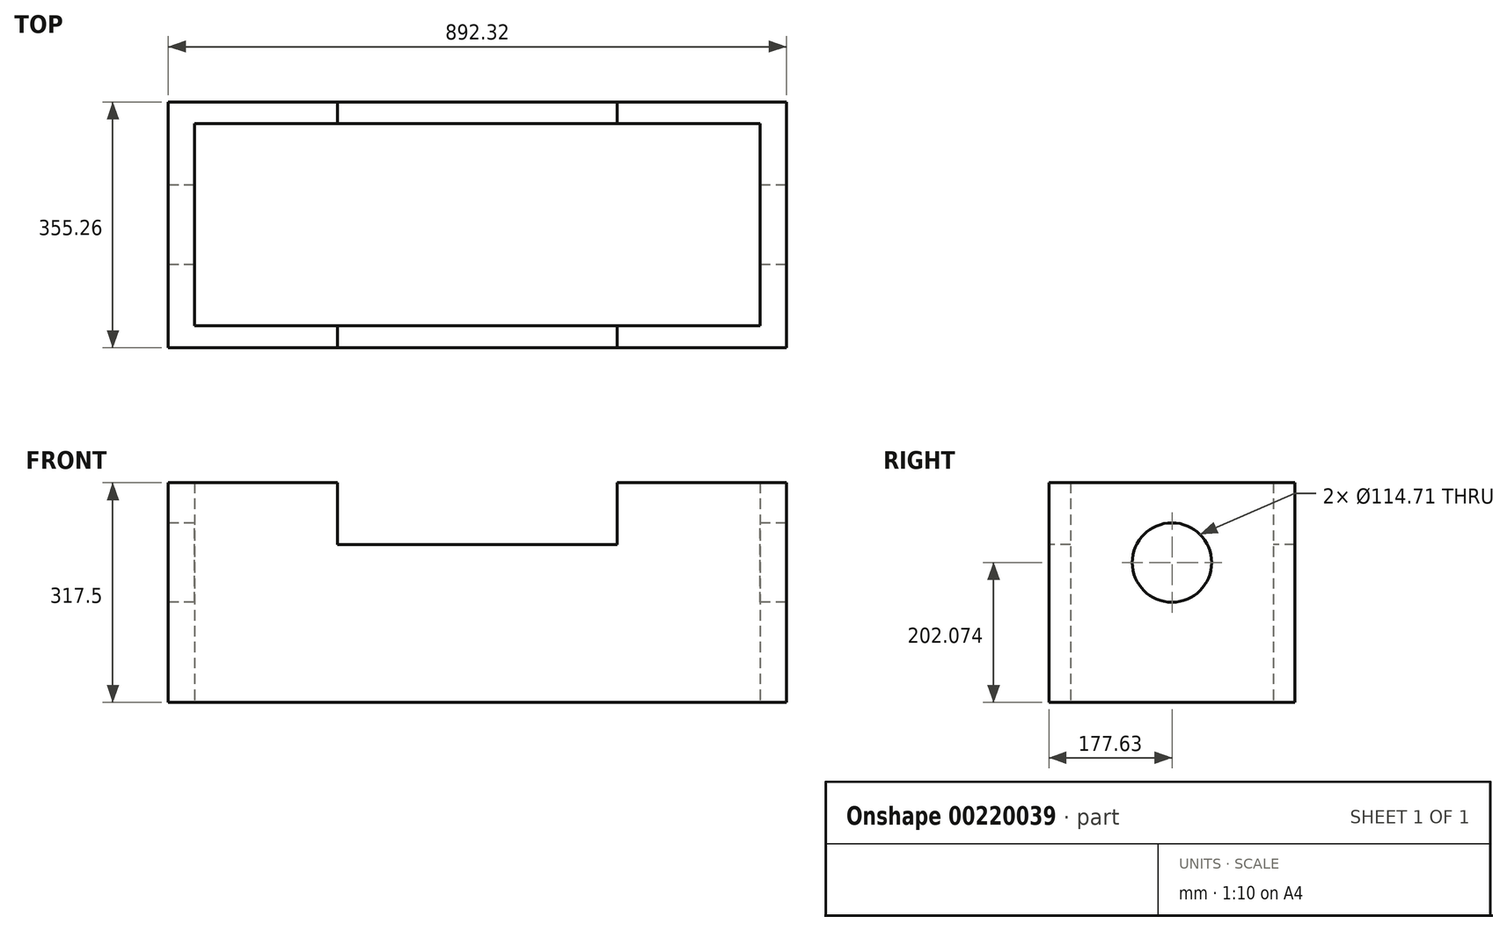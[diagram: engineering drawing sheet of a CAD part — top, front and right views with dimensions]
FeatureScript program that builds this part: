
annotation { "Feature Type Name" : "Feature", "Feature Type Description" : "" }
export const myFeature = defineFeature(function(context is Context, id is Id, definition is map)
    precondition{}
    {
        {
            var Q0;
            Q0=qCreatedBy(makeId("Top.planeOp"),FACE);
            var sketch = newSketch(context, id + "F0", { "sketchPlane" : qUnion([Q0])});
            skLineSegment(sketch, "E0.bottom", {"start": v(446.16, 177.63) * mm, "end": v(-446.16, 177.63) * mm});
            skLineSegment(sketch, "E0.top", {"start": v(446.16, -177.63) * mm, "end": v(-446.16, -177.63) * mm});
            skLineSegment(sketch, "E0.left", {"start": v(446.16, 177.63) * mm, "end": v(446.16, -177.63) * mm});
            skLineSegment(sketch, "E0.right", {"start": v(-446.16, 177.63) * mm, "end": v(-446.16, -177.63) * mm});
            skPoint(sketch, "E0.middle", {"position": v(0, 0) * mm});
            skLineSegment(sketch, "E1.bottom", {"start": v(408.33, 146.1) * mm, "end": v(-408.33, 146.1) * mm});
            skLineSegment(sketch, "E1.top", {"start": v(408.33, -146.1) * mm, "end": v(-408.33, -146.1) * mm});
            skLineSegment(sketch, "E1.left", {"start": v(408.33, 146.1) * mm, "end": v(408.33, -146.1) * mm});
            skLineSegment(sketch, "E1.right", {"start": v(-408.33, 146.1) * mm, "end": v(-408.33, -146.1) * mm});
            skSolve(sketch);
        }
        {
            var Q0;
            Q0=makeQuery(id+"F0.imprint","IMPRINT",FACE,{"disambiguationData":[TD([[makeQuery(id+"F0.imprint","IMPRINT",EDGE,{"derivedFrom":sQuery(id+"F0.wireOp",EDGE,"E0.bottom")}),1.0]])]});
            extrude(context, id + "F1", {"entities" : qUnion([Q0]), "depth" : 317.5 * mm});
        }
        {
            var Q0;
            Q0=makeQuery(id+"F1.opExtrude","SWEPT_FACE",FACE,{"disambiguationData":[OSD([sQuery(id+"F0.wireOp",EDGE,"E0.top")])]});
            var sketch = newSketch(context, id + "F2", { "sketchPlane" : qUnion([Q0])});
            skLineSegment(sketch, "E2.bottom", {"start": v(202.05, 406.8) * mm, "end": v(-202.05, 406.8) * mm});
            skLineSegment(sketch, "E2.top", {"start": v(202.05, 228.2) * mm, "end": v(-202.05, 228.2) * mm});
            skLineSegment(sketch, "E2.left", {"start": v(202.05, 406.8) * mm, "end": v(202.05, 228.2) * mm});
            skLineSegment(sketch, "E2.right", {"start": v(-202.05, 406.8) * mm, "end": v(-202.05, 228.2) * mm});
            skPoint(sketch, "E2.middle", {"position": v(0, 317.5) * mm});
            skSolve(sketch);
        }
        {
            var Q0;
            Q0 = qSketchRegion(id + "F2", true);
            extrude(context, id + "F3", {"entities" : qUnion([Q0]), "operationType" : NewBodyOperationType.REMOVE, "endBound" : BoundingType.THROUGH_ALL, "oppositeDirection" : true, "depth" : 25.4 * mm});
        }
        {
            var Q0;
            Q0=makeQuery(id+"F1.opExtrude","SWEPT_FACE",FACE,{"disambiguationData":[OSD([sQuery(id+"F0.wireOp",EDGE,"E0.right")])]});
            var sketch = newSketch(context, id + "F4", { "sketchPlane" : qUnion([Q0])});
            skCircle(sketch, "E3", {"center": v(0, 202.07) * mm, "radius": 57.35 * mm});
            skSolve(sketch);
        }
        {
            var Q0;
            Q0 = qSketchRegion(id + "F4", true);
            extrude(context, id + "F5", {"entities" : qUnion([Q0]), "operationType" : NewBodyOperationType.REMOVE, "endBound" : BoundingType.THROUGH_ALL, "oppositeDirection" : true, "depth" : 25.4 * mm});
        }
    });
